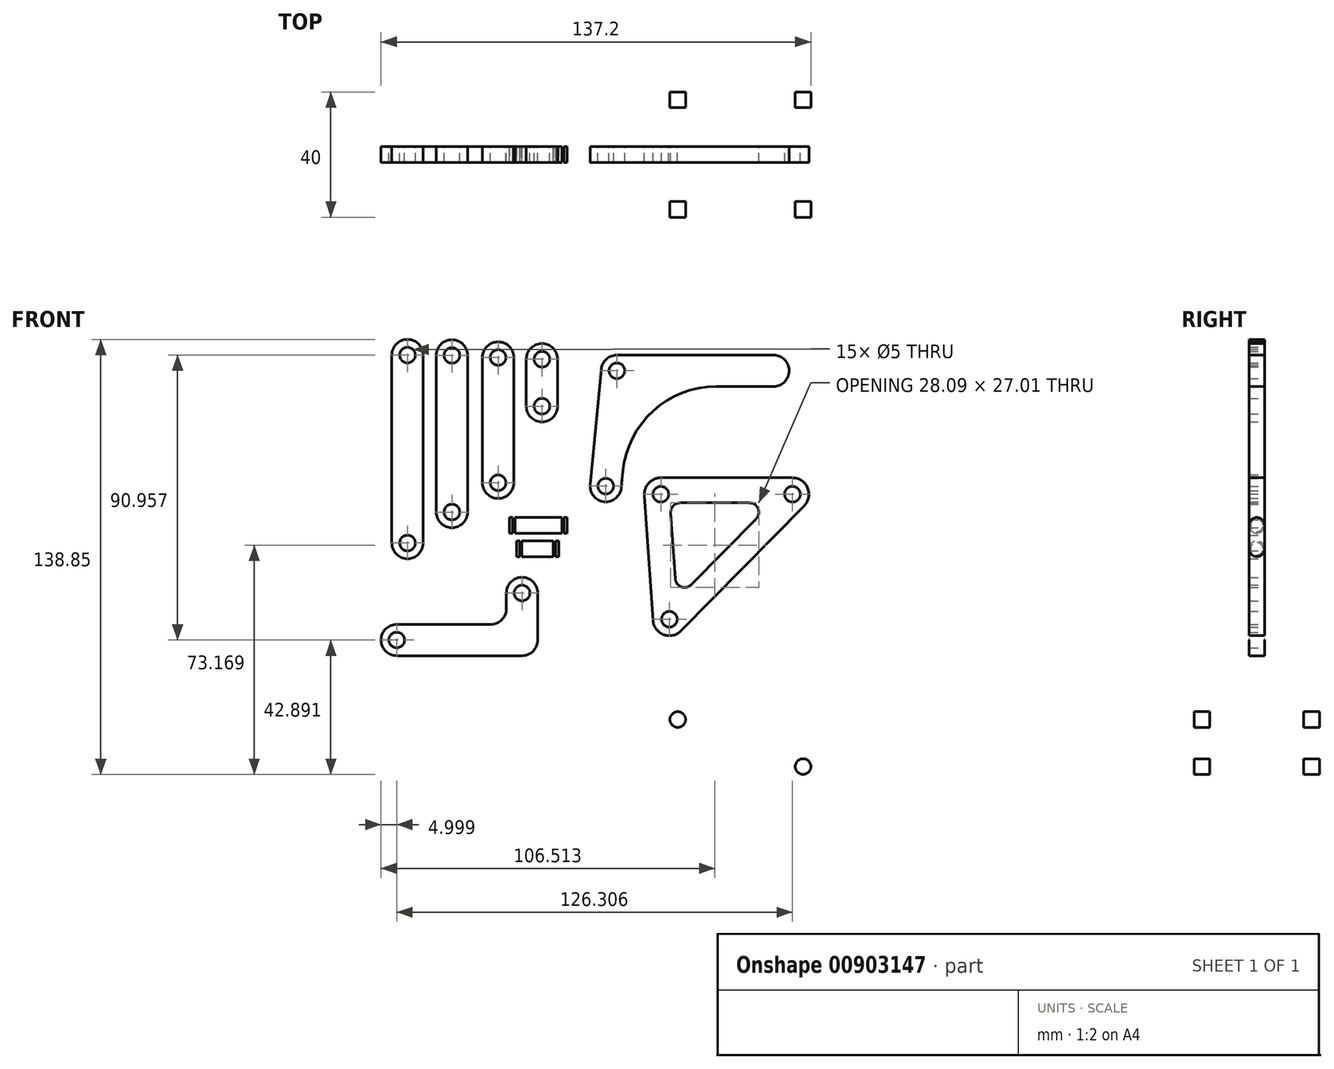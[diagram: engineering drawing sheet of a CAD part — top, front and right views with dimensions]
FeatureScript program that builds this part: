
annotation { "Feature Type Name" : "Feature", "Feature Type Description" : "" }
export const myFeature = defineFeature(function(context is Context, id is Id, definition is map)
    precondition{}
    {
        {
            assignVariable(context, id + "F0", {"name" : "T", "anyValue" : 5});
        }
        {
            assignVariable(context, id + "F1", {"name" : "W", "anyValue" : 40});
        }
        {
            var Q0;
            Q0=qCreatedBy(makeId("Front.planeOp"),FACE);
            var sketch = newSketch(context, id + "F2", { "sketchPlane" : qUnion([Q0])});
            skLineSegment(sketch, "E0", {"start": v(-8.35, 51.22) * mm, "end": v(-8.35, 66.22) * mm});
            skLineSegment(sketch, "E1", {"start": v(-18.35, 51.22) * mm, "end": v(-18.35, 66.22) * mm});
            skArc(sketch, "E2", {"start": v(-8.35, 66.22) * mm, "mid": v(-13.35, 71.22) * mm, "end": v(-18.35, 66.22) * mm});
            skArc(sketch, "E3", {"start": v(-18.35, 51.22) * mm, "mid": v(-13.35, 46.22) * mm, "end": v(-8.35, 51.22) * mm});
            skCircle(sketch, "E4", {"center": v(-13.35, 66.22) * mm, "radius": 2.5 * mm});
            skCircle(sketch, "E5", {"center": v(-13.35, 51.22) * mm, "radius": 2.5 * mm});
            skSolve(sketch);
        }
        {
            var Q0;
            Q0=qSketchRegion(id+"F2",true);
            extrude(context, id + "F3", {"entities" : qUnion([Q0]), "endBound" : BoundingType.SYMMETRIC, "depth" : (getVariable(context, 'T')) * mm, "offsetDistance" : 25 * mm});
        }
        {
            var Q0;
            Q0=qCreatedBy(makeId("Front.planeOp"),FACE);
            var sketch = newSketch(context, id + "F4", { "sketchPlane" : qUnion([Q0])});
            skLineSegment(sketch, "E6", {"start": v(-32.34, 66.78) * mm, "end": v(-32.34, 26.78) * mm});
            skLineSegment(sketch, "E7", {"start": v(-22.34, 26.78) * mm, "end": v(-22.34, 66.78) * mm});
            skArc(sketch, "E8", {"start": v(-22.34, 66.78) * mm, "mid": v(-27.34, 71.78) * mm, "end": v(-32.34, 66.78) * mm});
            skArc(sketch, "E9", {"start": v(-32.34, 26.78) * mm, "mid": v(-27.34, 21.78) * mm, "end": v(-22.34, 26.78) * mm});
            skCircle(sketch, "E10", {"center": v(-27.34, 26.78) * mm, "radius": 2.5 * mm});
            skCircle(sketch, "E11", {"center": v(-27.34, 66.78) * mm, "radius": 2.5 * mm});
            skSolve(sketch);
        }
        {
            var Q0;
            Q0=qSketchRegion(id+"F4",true);
            extrude(context, id + "F5", {"entities" : qUnion([Q0]), "endBound" : BoundingType.SYMMETRIC, "depth" : (getVariable(context, 'T')) * mm, "offsetDistance" : 25 * mm});
        }
        {
            var Q0;
            Q0=qCreatedBy(makeId("Front.planeOp"),FACE);
            var sketch = newSketch(context, id + "F6", { "sketchPlane" : qUnion([Q0])});
            skLineSegment(sketch, "E12", {"start": v(-47.08, 67.45) * mm, "end": v(-47.08, 17.45) * mm});
            skLineSegment(sketch, "E13", {"start": v(-37.08, 67.45) * mm, "end": v(-37.08, 17.45) * mm});
            skArc(sketch, "E14", {"start": v(-47.08, 17.45) * mm, "mid": v(-42.08, 12.45) * mm, "end": v(-37.08, 17.45) * mm});
            skArc(sketch, "E15", {"start": v(-37.08, 67.45) * mm, "mid": v(-42.08, 72.45) * mm, "end": v(-47.08, 67.45) * mm});
            skCircle(sketch, "E16", {"center": v(-42.08, 67.45) * mm, "radius": 2.5 * mm});
            skCircle(sketch, "E17", {"center": v(-42.08, 17.45) * mm, "radius": 2.5 * mm});
            skSolve(sketch);
        }
        {
            var Q0;
            Q0=qSketchRegion(id+"F6",true);
            extrude(context, id + "F7", {"entities" : qUnion([Q0]), "endBound" : BoundingType.SYMMETRIC, "depth" : (getVariable(context, 'T')) * mm, "offsetDistance" : 25 * mm});
        }
        {
            var Q0;
            Q0=qCreatedBy(makeId("Front.planeOp"),FACE);
            var sketch = newSketch(context, id + "F8", { "sketchPlane" : qUnion([Q0])});
            skLineSegment(sketch, "E18", {"start": v(-61.26, 67.56) * mm, "end": v(-61.26, 7.56) * mm});
            skLineSegment(sketch, "E19", {"start": v(-51.26, 7.56) * mm, "end": v(-51.26, 67.56) * mm});
            skArc(sketch, "E20", {"start": v(-51.26, 67.56) * mm, "mid": v(-56.26, 72.56) * mm, "end": v(-61.26, 67.56) * mm});
            skArc(sketch, "E21", {"start": v(-61.26, 7.56) * mm, "mid": v(-56.26, 2.56) * mm, "end": v(-51.26, 7.56) * mm});
            skCircle(sketch, "E22", {"center": v(-56.26, 67.56) * mm, "radius": 2.5 * mm});
            skCircle(sketch, "E23", {"center": v(-56.26, 7.56) * mm, "radius": 2.5 * mm});
            skSolve(sketch);
        }
        {
            var Q0;
            Q0=qSketchRegion(id+"F8",true);
            extrude(context, id + "F9", {"entities" : qUnion([Q0]), "endBound" : BoundingType.SYMMETRIC, "depth" : (getVariable(context, 'T')) * mm, "offsetDistance" : 25 * mm});
        }
        {
            var Q0;
            Q0=qCreatedBy(makeId("Front.planeOp"),FACE);
            var sketch = newSketch(context, id + "F10", { "sketchPlane" : qUnion([Q0])});
            skLineSegment(sketch, "E24", {"start": v(60.57, 67.55) * mm, "end": v(10.57, 67.55) * mm});
            skLineSegment(sketch, "E25", {"start": v(5.6, 63.03) * mm, "end": v(2.04, 26.2) * mm});
            skLineSegment(sketch, "E26", {"start": v(12, 25.24) * mm, "end": v(12.5, 30.44) * mm});
            skLineSegment(sketch, "E27", {"start": v(42.35, 57.55) * mm, "end": v(60.57, 57.55) * mm});
            skArc(sketch, "E28", {"start": v(2.04, 26.2) * mm, "mid": v(6.53, 20.74) * mm, "end": v(12, 25.24) * mm});
            skArc(sketch, "E29", {"start": v(10.57, 67.55) * mm, "mid": v(7.21, 66.25) * mm, "end": v(5.6, 63.03) * mm});
            skArc(sketch, "E30", {"start": v(60.57, 57.55) * mm, "mid": v(65.57, 62.55) * mm, "end": v(60.57, 67.55) * mm});
            skArc(sketch, "E31", {"start": v(42.35, 57.55) * mm, "mid": v(22.19, 49.76) * mm, "end": v(12.5, 30.44) * mm});
            skCircle(sketch, "E32", {"center": v(7.01, 25.72) * mm, "radius": 2.5 * mm});
            skCircle(sketch, "E33", {"center": v(10.57, 62.55) * mm, "radius": 2.5 * mm});
            skSolve(sketch);
        }
        {
            var Q0;
            Q0=makeQuery(id+"F10.imprint","IMPRINT",FACE,{"disambiguationData":[TD([[makeQuery(id+"F10.imprint","IMPRINT",EDGE,{"derivedFrom":sQuery(id+"F10.wireOp",EDGE,"E24")}),1.0]])]});
            extrude(context, id + "F11", {"entities" : qUnion([Q0]), "endBound" : BoundingType.SYMMETRIC, "depth" : (getVariable(context, 'T')) * mm, "offsetDistance" : 25 * mm});
        }
        {
            var Q0;
            Q0=qCreatedBy(makeId("Front.planeOp"),FACE);
            var sketch = newSketch(context, id + "F12", { "sketchPlane" : qUnion([Q0])});
            skLineSegment(sketch, "E34", {"start": v(19.37, 22.78) * mm, "end": v(22.08, -17.13) * mm});
            skLineSegment(sketch, "E35", {"start": v(31.06, -20.46) * mm, "end": v(70.35, 19.45) * mm});
            skLineSegment(sketch, "E36", {"start": v(66.6, 28.38) * mm, "end": v(24.6, 28.38) * mm});
            skArc(sketch, "E37", {"start": v(24.6, 28.38) * mm, "mid": v(20.77, 26.72) * mm, "end": v(19.37, 22.78) * mm});
            skArc(sketch, "E38", {"start": v(22.08, -17.13) * mm, "mid": v(25.5, -21.7) * mm, "end": v(31.06, -20.46) * mm});
            skArc(sketch, "E39", {"start": v(70.35, 19.45) * mm, "mid": v(71.45, 25.16) * mm, "end": v(66.6, 28.38) * mm});
            skCircle(sketch, "E40", {"center": v(24.6, 23.13) * mm, "radius": 2.5 * mm});
            skCircle(sketch, "E41", {"center": v(27.32, -16.77) * mm, "radius": 2.5 * mm});
            skCircle(sketch, "E42", {"center": v(66.6, 23.13) * mm, "radius": 2.5 * mm});
            skLineSegment(sketch, "E43", {"start": v(30.76, 20.38) * mm, "end": v(52.88, 20.38) * mm});
            skLineSegment(sketch, "E44", {"start": v(55.01, 15.28) * mm, "end": v(34.33, -5.74) * mm});
            skLineSegment(sketch, "E45", {"start": v(27.77, 17.18) * mm, "end": v(29.2, -3.83) * mm});
            skArc(sketch, "E46", {"start": v(29.2, -3.83) * mm, "mid": v(31.15, -6.44) * mm, "end": v(34.33, -5.74) * mm});
            skArc(sketch, "E47", {"start": v(30.76, 20.38) * mm, "mid": v(28.57, 19.43) * mm, "end": v(27.77, 17.18) * mm});
            skArc(sketch, "E48", {"start": v(55.01, 15.28) * mm, "mid": v(55.64, 18.54) * mm, "end": v(52.88, 20.38) * mm});
            skLineSegment(sketch, "E49", {"start": v(52.88, 28.38) * mm, "end": v(52.88, 20.38) * mm, "construction": true});
            skLineSegment(sketch, "E50", {"start": v(60.71, 9.67) * mm, "end": v(55.01, 15.28) * mm, "construction": true});
            skLineSegment(sketch, "E51", {"start": v(19.78, 16.64) * mm, "end": v(27.77, 17.18) * mm, "construction": true});
            skSolve(sketch);
        }
        {
            var Q0;
            Q0=qSketchRegion(id+"F12",true);
            extrude(context, id + "F13", {"entities" : qUnion([Q0]), "endBound" : BoundingType.SYMMETRIC, "depth" : (getVariable(context, 'T')) * mm, "offsetDistance" : 25 * mm});
        }
        {
            var Q0;
            Q0=qCreatedBy(makeId("Front.planeOp"),FACE);
            var sketch = newSketch(context, id + "F14", { "sketchPlane" : qUnion([Q0])});
            skLineSegment(sketch, "E52", {"start": v(-21.44, 5.72) * mm, "end": v(-21.44, 8.22) * mm});
            skLineSegment(sketch, "E53", {"start": v(-21.44, 8.22) * mm, "end": v(-20.44, 8.22) * mm});
            skLineSegment(sketch, "E54", {"start": v(-20.44, 8.22) * mm, "end": v(-20.44, 7.72) * mm});
            skLineSegment(sketch, "E55", {"start": v(-20.44, 7.72) * mm, "end": v(-19.74, 7.72) * mm});
            skLineSegment(sketch, "E56", {"start": v(-19.74, 7.72) * mm, "end": v(-19.74, 8.22) * mm});
            skLineSegment(sketch, "E57", {"start": v(-19.74, 8.22) * mm, "end": v(-9.74, 8.22) * mm});
            skLineSegment(sketch, "E58", {"start": v(-9.74, 8.22) * mm, "end": v(-9.74, 7.72) * mm});
            skLineSegment(sketch, "E59", {"start": v(-9.74, 7.72) * mm, "end": v(-9.04, 7.72) * mm});
            skLineSegment(sketch, "E60", {"start": v(-9.04, 7.72) * mm, "end": v(-9.04, 8.22) * mm});
            skLineSegment(sketch, "E61", {"start": v(-9.04, 8.22) * mm, "end": v(-8.04, 8.22) * mm});
            skLineSegment(sketch, "E62", {"start": v(-8.04, 8.22) * mm, "end": v(-8.04, 5.72) * mm});
            skLineSegment(sketch, "E63", {"start": v(-8.04, 5.72) * mm, "end": v(-21.44, 5.72) * mm});
            skSolve(sketch);
        }
        {
            var Q0;
            Q0=makeQuery(id+"F14.imprint","IMPRINT",FACE,{"disambiguationData":[TD([[makeQuery(id+"F14.imprint","IMPRINT",EDGE,{"derivedFrom":sQuery(id+"F14.wireOp",EDGE,"E52")}),-1.0]])]});
            var Q1;
            Q1=sQuery(id+"F14.wireOp",EDGE,"E63");
            revolve(context, id + "F15", {"surfaceOperationType" : NewSurfaceOperationType.NEW, "entities" : qUnion([Q0]), "axis" : qUnion([Q1]), "revolveType" : RevolveType.FULL});
        }
        {
            var Q0;
            Q0=qCreatedBy(makeId("Front.planeOp"),FACE);
            var sketch = newSketch(context, id + "F16", { "sketchPlane" : qUnion([Q0])});
            skLineSegment(sketch, "E64", {"start": v(-23.7, 15.7) * mm, "end": v(-23.7, 13.2) * mm});
            skLineSegment(sketch, "E65", {"start": v(-23.7, 13.2) * mm, "end": v(-5.3, 13.2) * mm});
            skLineSegment(sketch, "E66", {"start": v(-5.3, 13.2) * mm, "end": v(-5.3, 15.7) * mm});
            skLineSegment(sketch, "E67", {"start": v(-5.3, 15.7) * mm, "end": v(-6.3, 15.7) * mm});
            skLineSegment(sketch, "E68", {"start": v(-6.3, 15.7) * mm, "end": v(-6.3, 15.2) * mm});
            skLineSegment(sketch, "E69", {"start": v(-6.3, 15.2) * mm, "end": v(-7, 15.2) * mm});
            skLineSegment(sketch, "E70", {"start": v(-7, 15.2) * mm, "end": v(-7, 15.7) * mm});
            skLineSegment(sketch, "E71", {"start": v(-7, 15.7) * mm, "end": v(-22, 15.7) * mm});
            skLineSegment(sketch, "E72", {"start": v(-22, 15.7) * mm, "end": v(-22, 15.2) * mm});
            skLineSegment(sketch, "E73", {"start": v(-22, 15.2) * mm, "end": v(-22.7, 15.2) * mm});
            skLineSegment(sketch, "E74", {"start": v(-22.7, 15.2) * mm, "end": v(-22.7, 15.7) * mm});
            skLineSegment(sketch, "E75", {"start": v(-22.7, 15.7) * mm, "end": v(-23.7, 15.7) * mm});
            skSolve(sketch);
        }
        {
            var Q0;
            Q0=qSketchRegion(id+"F16",true);
            var Q1;
            Q1=sQuery(id+"F16.wireOp",EDGE,"E65");
            revolve(context, id + "F17", {"surfaceOperationType" : NewSurfaceOperationType.NEW, "entities" : qUnion([Q0]), "axis" : qUnion([Q1]), "revolveType" : RevolveType.FULL});
        }
        {
            var Q0;
            Q0=qCreatedBy(makeId("Front.planeOp"),FACE);
            var sketch = newSketch(context, id + "F18", { "sketchPlane" : qUnion([Q0])});
            skLineSegment(sketch, "E76", {"start": v(-59.7, -18.4) * mm, "end": v(-29.7, -18.4) * mm});
            skLineSegment(sketch, "E77", {"start": v(-24.7, -13.4) * mm, "end": v(-24.7, -8.4) * mm});
            skLineSegment(sketch, "E78", {"start": v(-14.7, -8.4) * mm, "end": v(-14.7, -23.4) * mm});
            skLineSegment(sketch, "E79", {"start": v(-19.7, -28.4) * mm, "end": v(-59.7, -28.4) * mm});
            skArc(sketch, "E80", {"start": v(-59.7, -18.4) * mm, "mid": v(-64.7, -23.4) * mm, "end": v(-59.7, -28.4) * mm});
            skArc(sketch, "E81", {"start": v(-14.7, -8.4) * mm, "mid": v(-19.7, -3.4) * mm, "end": v(-24.7, -8.4) * mm});
            skPoint(sketch, "E82.visualSharp", {"position": v(-24.7, -18.4) * mm});
            skArc(sketch, "E82.filletArc", {"start": v(-29.7, -18.4) * mm, "mid": v(-26.17, -16.93) * mm, "end": v(-24.7, -13.4) * mm});
            skPoint(sketch, "E83.visualSharp", {"position": v(-14.7, -28.4) * mm});
            skArc(sketch, "E83.filletArc", {"start": v(-19.7, -28.4) * mm, "mid": v(-16.17, -26.93) * mm, "end": v(-14.7, -23.4) * mm});
            skCircle(sketch, "E84", {"center": v(-59.7, -23.4) * mm, "radius": 2.5 * mm});
            skCircle(sketch, "E85", {"center": v(-19.7, -8.4) * mm, "radius": 2.5 * mm});
            skSolve(sketch);
        }
        {
            var Q0;
            Q0=qSketchRegion(id+"F18",true);
            extrude(context, id + "F19", {"entities" : qUnion([Q0]), "endBound" : BoundingType.SYMMETRIC, "depth" : (getVariable(context, 'T')) * mm, "offsetDistance" : 25 * mm});
        }
        {
            var Q0;
            Q0=qCreatedBy(makeId("Front.planeOp"),FACE);
            var sketch = newSketch(context, id + "F20", { "sketchPlane" : qUnion([Q0])});
            skLineSegment(sketch, "E86.bottom", {"start": v(-80, -39.79) * mm, "end": v(80, -39.79) * mm});
            skLineSegment(sketch, "E86.top", {"start": v(-80, -69.79) * mm, "end": v(80, -69.79) * mm});
            skLineSegment(sketch, "E86.left", {"start": v(-80, -39.79) * mm, "end": v(-80, -69.79) * mm});
            skLineSegment(sketch, "E86.right", {"start": v(80, -39.79) * mm, "end": v(80, -69.79) * mm});
            skSolve(sketch);
        }
        {
            var Q0;
            Q0=makeQuery(id+"F20.imprint","IMPRINT",FACE,{"disambiguationData":[TD([[makeQuery(id+"F20.imprint","IMPRINT",EDGE,{"derivedFrom":sQuery(id+"F20.wireOp",EDGE,"E86.bottom")}),-1.0]])]});
            extrude(context, id + "F21", {"entities" : qUnion([Q0]), "endBound" : BoundingType.SYMMETRIC, "depth" : (getVariable(context, 'W')) * mm, "offsetDistance" : 25 * mm});
        }
        {
            var Q0;
            Q0=makeQuery(id+"F21.opExtrude","SWEPT_FACE",FACE,{"disambiguationData":[OSD([sQuery(id+"F20.wireOp",EDGE,"E86.bottom")])]});
            var Q1;
            Q1=makeQuery(id+"F21.opExtrude","SWEPT_FACE",FACE,{"disambiguationData":[OSD([sQuery(id+"F20.wireOp",EDGE,"E86.top")])]});
            shell(context, id + "F22", {"entities" : qUnion([Q0, Q1]), "thickness" : (getVariable(context, 'T')) * mm});
        }
        {
            var Q0;
            Q0=makeQuery(id+"F21.opExtrude","CAP_FACE",FACE,{"disambiguationData":[OSD([sQuery(id+"F20.wireOp",EDGE,"E86.bottom"),sQuery(id+"F20.wireOp",EDGE,"E86.top"),sQuery(id+"F20.wireOp",EDGE,"E86.left"),sQuery(id+"F20.wireOp",EDGE,"E86.right")])],"isStart":false});
            var sketch = newSketch(context, id + "F23", { "sketchPlane" : qUnion([Q0])});
            skCircle(sketch, "E87", {"center": v(-70, -63.79) * mm, "radius": 2.5 * mm});
            skCircle(sketch, "E88", {"center": v(-30, -48.79) * mm, "radius": 2.5 * mm});
            skLineSegment(sketch, "E89", {"start": v(-70, -63.79) * mm, "end": v(-30, -63.79) * mm, "construction": true});
            skLineSegment(sketch, "E90", {"start": v(-30, -63.79) * mm, "end": v(-30, -48.79) * mm, "construction": true});
            skCircle(sketch, "E91.MirrorC", {"center": v(30, -48.79) * mm, "radius": 2.5 * mm});
            skCircle(sketch, "E92.MirrorC", {"center": v(70, -63.79) * mm, "radius": 2.5 * mm});
            skSolve(sketch);
        }
        {
            var Q0;
            Q0=makeQuery(id+"F23.imprint","IMPRINT",FACE,{"disambiguationData":[TD([[makeQuery(id+"F23.imprint","IMPRINT",EDGE,{"derivedFrom":sQuery(id+"F23.wireOp",EDGE,"E87")}),1.0]])]});
            var Q1;
            Q1=makeQuery(id+"F23.imprint","IMPRINT",FACE,{"disambiguationData":[TD([[makeQuery(id+"F23.imprint","IMPRINT",EDGE,{"derivedFrom":sQuery(id+"F23.wireOp",EDGE,"E88")}),1.0]])]});
            var Q2;
            Q2=makeQuery(id+"F23.imprint","IMPRINT",FACE,{"disambiguationData":[TD([[makeQuery(id+"F23.imprint","IMPRINT",EDGE,{"derivedFrom":sQuery(id+"F23.wireOp",EDGE,"E91.MirrorC")}),-1.0]])]});
            var Q3;
            Q3=makeQuery(id+"F23.imprint","IMPRINT",FACE,{"disambiguationData":[TD([[makeQuery(id+"F23.imprint","IMPRINT",EDGE,{"derivedFrom":sQuery(id+"F23.wireOp",EDGE,"E92.MirrorC")}),-1.0]])]});
            var Q4;
            Q4=makeQuery(id+"F21.opExtrude","CAP_FACE",FACE,{"disambiguationData":[OSD([sQuery(id+"F20.wireOp",EDGE,"E86.bottom"),sQuery(id+"F20.wireOp",EDGE,"E86.top"),sQuery(id+"F20.wireOp",EDGE,"E86.left"),sQuery(id+"F20.wireOp",EDGE,"E86.right")])],"isStart":true});
            extrude(context, id + "F24", {"entities" : qUnion([Q0, Q1, Q2, Q3]), "operationType" : NewBodyOperationType.REMOVE, "endBound" : BoundingType.UP_TO_SURFACE, "oppositeDirection" : true, "depth" : 25 * mm, "endBoundEntityFace" : qUnion([Q4]), "offsetDistance" : 25 * mm});
        }
    });
